# Revit family: ASL_64_Series_Timber_Door_40mm_Head
name_source: partatom
category: Detail Items
revit_build: Autodesk Revit 2018 (Build: 20170223_1515(x64)
units: mm (PartAtom-declared; Revit-internal decimal feet)

## family parameters
Rotate with component = No
Section Shape = Not Defined
Shared = Yes

## types (4) — shared parameters
Door Depth = 51 mm  [stored 0.167323 ft]
Door Stop_ASL_545 = No
Flush Infill_ASL_648 = No
Head Depth = 26 mm
Headsection_ASL_400 = No
Headsection_ASL_405a = Yes
Manufacturer = Aluminate Solutions Limited
Pocket Starter Cap_ASL_537 = Yes
Reven Seal = Yes
Technical Info = www.aluminate.nz

## per-type parameters (varying)
| type | Door_40 | Glazing | Pocket Starter Cap_ASL_543 | Type Comments |
| Double Action Door 40mm | Yes | No | No | ASL 64 Series Head With Double Action 40mm Timber Door |
| Single Action Door 40mm | Yes | No | No | ASL 64 Series Head With Single Action 40mm Timber Door |
| Single Action Raven Seal Door 40mm | Yes | No | No | ASL 64 Series Head With Single Action Raven Seal 40mm Timber Door |
| Glazing | No | Yes | Yes | ASL 64 Series Head With Glazing |

note: [stored X ft] marks values corroborated as IEEE doubles in the binary element streams (Revit-internal decimal feet)

## geometry (parser evidence)
native form markers: Sweep x9
no freeform markers — native parametric forms only
